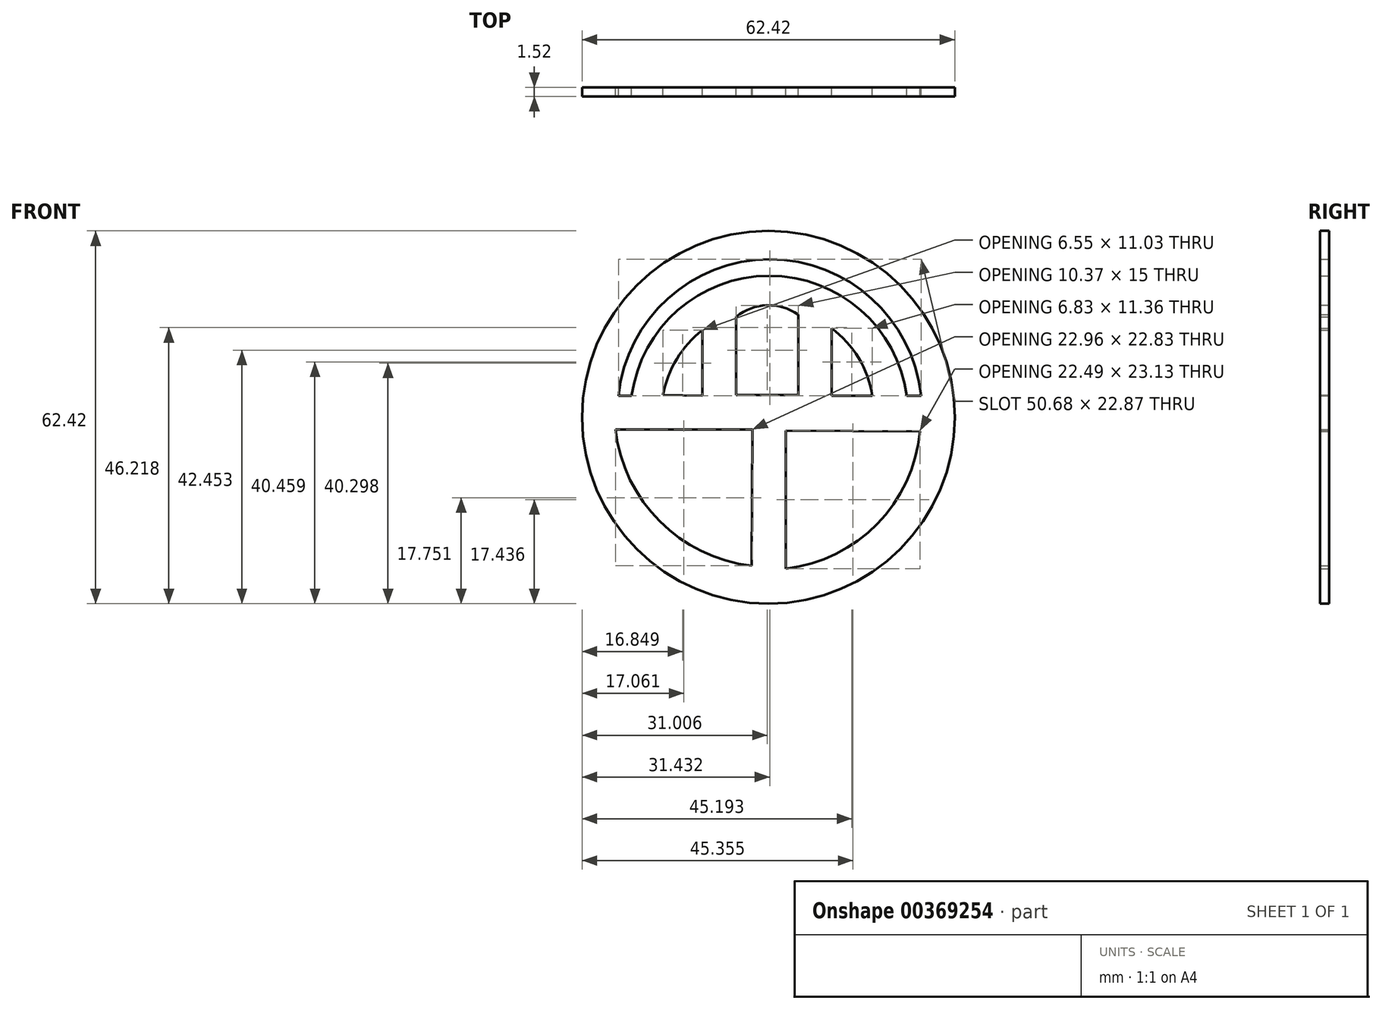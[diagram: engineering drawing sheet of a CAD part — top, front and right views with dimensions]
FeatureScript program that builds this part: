
annotation { "Feature Type Name" : "Feature", "Feature Type Description" : "" }
export const myFeature = defineFeature(function(context is Context, id is Id, definition is map)
    precondition{}
    {
        {
            var Q0;
            Q0=qCreatedBy(makeId("Front.planeOp"),FACE);
            var sketch = newSketch(context, id + "F0", { "sketchPlane" : qUnion([Q0])});
            skCircle(sketch, "E0", {"center": v(0, 0) * mm, "radius": 31.2 * mm});
            skArc(sketch, "E1", {"start": v(25.56, 3.57) * mm, "mid": v(0.22, 26.44) * mm, "end": v(-25.12, 3.57) * mm});
            skArc(sketch, "E2", {"start": v(23.18, 3.57) * mm, "mid": v(0.14, 23.7) * mm, "end": v(-22.9, 3.57) * mm});
            skLineSegment(sketch, "E3", {"start": v(-22.9, 3.57) * mm, "end": v(-25.12, 3.57) * mm});
            skLineSegment(sketch, "E4", {"start": v(23.18, 3.57) * mm, "end": v(25.56, 3.57) * mm});
            skArc(sketch, "E5", {"start": v(-17.64, 3.74) * mm, "mid": v(-15.35, 9.77) * mm, "end": v(-11.09, 14.6) * mm});
            skLineSegment(sketch, "E6", {"start": v(-11.09, 14.6) * mm, "end": v(-11.09, 3.57) * mm});
            skLineSegment(sketch, "E7", {"start": v(-11.09, 3.57) * mm, "end": v(-17.64, 3.74) * mm});
            skLineSegment(sketch, "E8", {"start": v(-5.4, 3.74) * mm, "end": v(4.98, 3.74) * mm});
            skLineSegment(sketch, "E9", {"start": v(4.98, 3.74) * mm, "end": v(4.98, 17.18) * mm});
            skLineSegment(sketch, "E10", {"start": v(-5.4, 3.74) * mm, "end": v(-5.4, 16.84) * mm});
            skArc(sketch, "E11", {"start": v(4.98, 17.18) * mm, "mid": v(-0.26, 18.74) * mm, "end": v(-5.4, 16.84) * mm});
            skArc(sketch, "E12", {"start": v(17.4, 3.57) * mm, "mid": v(15.1, 9.93) * mm, "end": v(10.57, 14.93) * mm});
            skLineSegment(sketch, "E13", {"start": v(10.57, 14.93) * mm, "end": v(10.57, 3.57) * mm});
            skLineSegment(sketch, "E14", {"start": v(10.57, 3.57) * mm, "end": v(17.4, 3.57) * mm});
            skArc(sketch, "E15", {"start": v(-25.63, -2.04) * mm, "mid": v(-18.19, -17.43) * mm, "end": v(-2.8, -24.88) * mm});
            skLineSegment(sketch, "E16", {"start": v(-25.63, -2.04) * mm, "end": v(-2.67, -2.04) * mm});
            skLineSegment(sketch, "E17", {"start": v(-2.67, -2.04) * mm, "end": v(-2.8, -24.88) * mm});
            skArc(sketch, "E18", {"start": v(25.4, -2.38) * mm, "mid": v(18.22, -17.85) * mm, "end": v(2.9, -25.34) * mm});
            skLineSegment(sketch, "E19", {"start": v(2.9, -25.34) * mm, "end": v(2.9, -2.21) * mm});
            skLineSegment(sketch, "E20", {"start": v(2.9, -2.21) * mm, "end": v(25.4, -2.38) * mm});
            skSolve(sketch);
        }
        {
            var Q0;
            Q0 = qSketchRegion(id + "F0", true);
            extrude(context, id + "F1", {"entities" : qUnion([Q0]), "depth" : 1.52 * mm});
        }
    });
